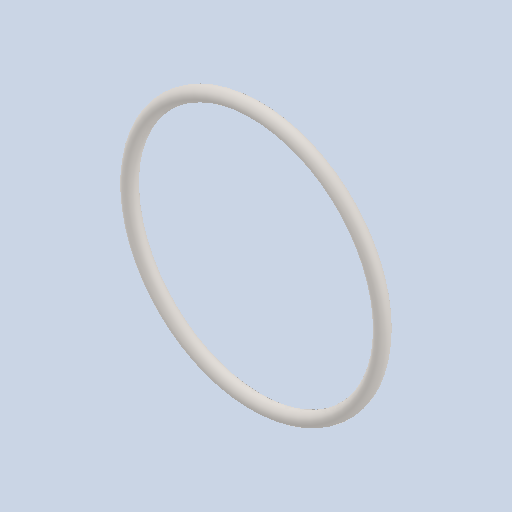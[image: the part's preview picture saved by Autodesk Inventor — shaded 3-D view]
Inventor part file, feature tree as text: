
AUTODESK INVENTOR PART (.ipt)
format: ipt  version: 2024.1 (Build 281209000, 209)  size: 114,176 bytes
history: native  units: in
note: dims shown in document units (in); Inventor stores cm internally (conversion verified against a paired STEP export)
features: sweep x1
ambient origin geometry x8: Origin, YZ Plane, XZ Plane, XY Plane, X Axis, Y Axis, Z Axis, Center Point
bodies: Solid1 (feature_tree)
feature tree (1):
  sweep  "Sweep1"
